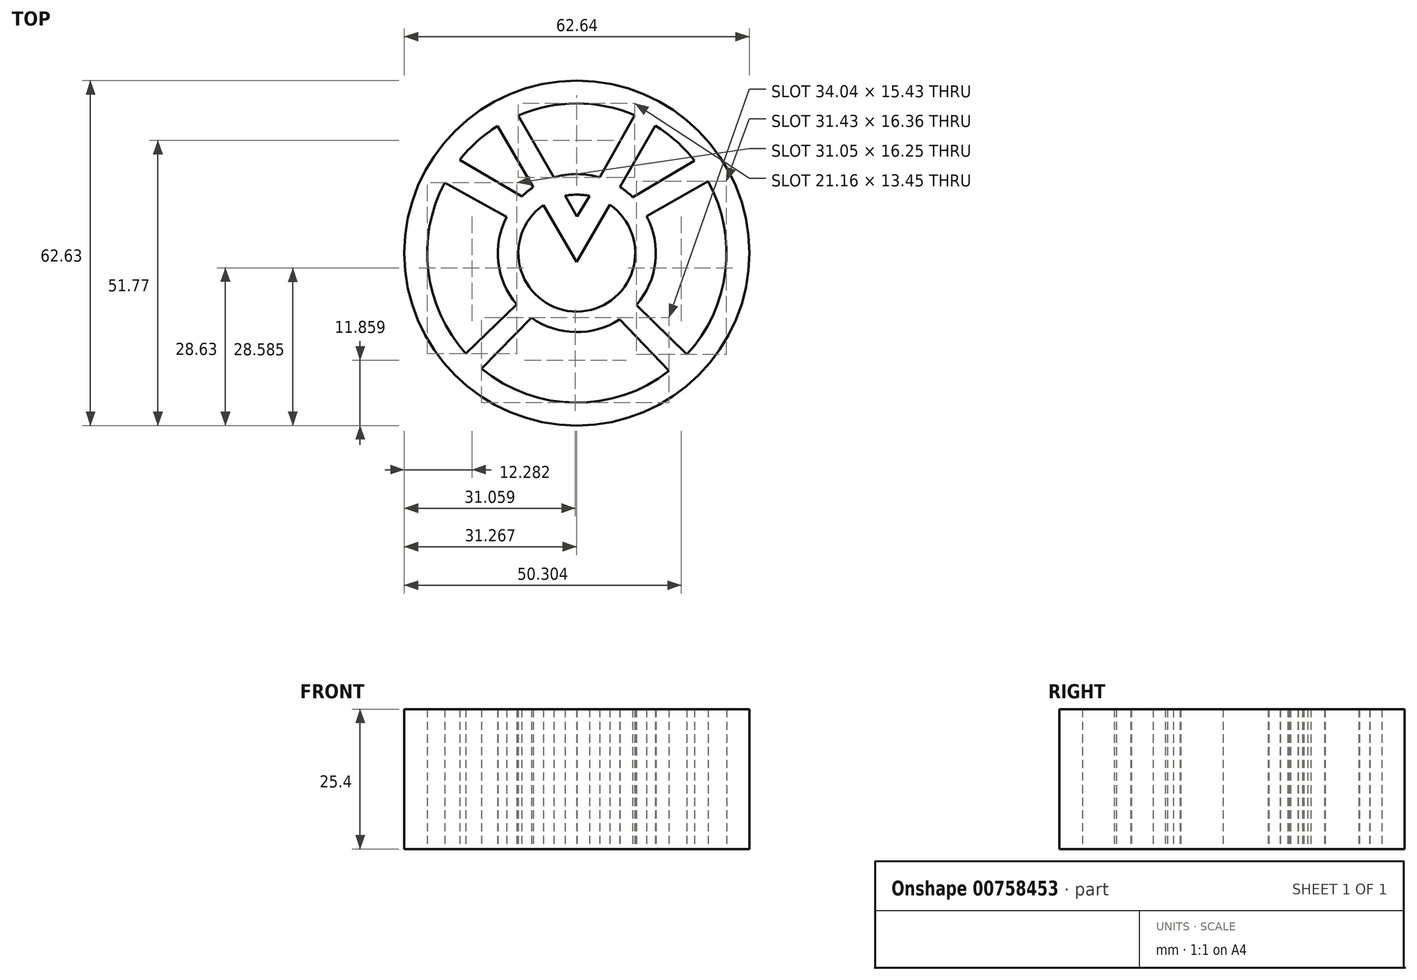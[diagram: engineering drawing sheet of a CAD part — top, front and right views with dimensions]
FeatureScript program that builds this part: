
annotation { "Feature Type Name" : "Feature", "Feature Type Description" : "" }
export const myFeature = defineFeature(function(context is Context, id is Id, definition is map)
    precondition{}
    {
        {
            var Q0;
            Q0=qCreatedBy(makeId("Top.planeOp"),FACE);
            var sketch = newSketch(context, id + "F0", { "sketchPlane" : qUnion([Q0])});
            skCircle(sketch, "E0", {"center": v(33.81, 37.33) * mm, "radius": 31.32 * mm});
            skArc(sketch, "E1", {"start": v(55.2, 54.1) * mm, "mid": v(51.91, 57.6) * mm, "end": v(48.06, 60.47) * mm});
            skLineSegment(sketch, "E2", {"start": v(48.06, 60.47) * mm, "end": v(41.65, 49.34) * mm});
            skLineSegment(sketch, "E3", {"start": v(33.81, 35.72) * mm, "end": v(27.77, 46.06) * mm});
            skArc(sketch, "E4", {"start": v(27.77, 46.06) * mm, "mid": v(33.85, 26.7) * mm, "end": v(39.79, 46.1) * mm});
            skArc(sketch, "E5", {"start": v(25.88, 49.29) * mm, "mid": v(24.8, 48.5) * mm, "end": v(23.8, 47.61) * mm});
            skLineSegment(sketch, "E6", {"start": v(23.18, 62.34) * mm, "end": v(29.66, 51.06) * mm});
            skLineSegment(sketch, "E7", {"start": v(44.33, 62.38) * mm, "end": v(37.98, 51.06) * mm});
            skLineSegment(sketch, "E8", {"start": v(55.2, 54.1) * mm, "end": v(43.95, 47.48) * mm});
            skLineSegment(sketch, "E9", {"start": v(57.66, 50.35) * mm, "end": v(46.5, 44.03) * mm});
            skLineSegment(sketch, "E10", {"start": v(53.8, 18.93) * mm, "end": v(44.62, 27.89) * mm});
            skLineSegment(sketch, "E11", {"start": v(50.57, 15.93) * mm, "end": v(41.57, 25.26) * mm});
            skLineSegment(sketch, "E12", {"start": v(16.53, 16.35) * mm, "end": v(25.56, 25.58) * mm});
            skLineSegment(sketch, "E13", {"start": v(13.68, 19.07) * mm, "end": v(22.9, 28.01) * mm});
            skLineSegment(sketch, "E14", {"start": v(21.07, 43.92) * mm, "end": v(9.83, 50.12) * mm});
            skLineSegment(sketch, "E15", {"start": v(12.54, 54.24) * mm, "end": v(23.8, 47.61) * mm});
            skLineSegment(sketch, "E16.trimOffspring", {"start": v(25.88, 49.29) * mm, "end": v(19.4, 60.37) * mm});
            skLineSegment(sketch, "E17", {"start": v(31.71, 47.74) * mm, "end": v(33.82, 43.96) * mm});
            skLineSegment(sketch, "E18", {"start": v(33.82, 43.96) * mm, "end": v(36.12, 47.7) * mm});
            skArc(sketch, "E19.trimOffspring", {"start": v(36.12, 47.7) * mm, "mid": v(33.92, 47.94) * mm, "end": v(31.71, 47.74) * mm});
            skLineSegment(sketch, "E20.trimOffspring", {"start": v(39.79, 46.1) * mm, "end": v(33.81, 35.72) * mm});
            skArc(sketch, "E21.trimOffspring", {"start": v(37.98, 51.06) * mm, "mid": v(33.82, 51.68) * mm, "end": v(29.66, 51.06) * mm});
            skArc(sketch, "E22.trimOffspring", {"start": v(43.95, 47.48) * mm, "mid": v(42.85, 48.47) * mm, "end": v(41.65, 49.34) * mm});
            skArc(sketch, "E23.trimOffspring", {"start": v(21.07, 43.92) * mm, "mid": v(19.56, 35.69) * mm, "end": v(22.9, 28.01) * mm});
            skArc(sketch, "E24.trimOffspring", {"start": v(44.62, 27.89) * mm, "mid": v(48.06, 35.67) * mm, "end": v(46.5, 44.03) * mm});
            skArc(sketch, "E25.trimOffspring", {"start": v(25.56, 25.58) * mm, "mid": v(33.52, 22.98) * mm, "end": v(41.57, 25.26) * mm});
            skArc(sketch, "E26.trimOffspring", {"start": v(44.33, 62.38) * mm, "mid": v(33.75, 64.5) * mm, "end": v(23.18, 62.34) * mm});
            skArc(sketch, "E27.trimOffspring", {"start": v(19.4, 60.37) * mm, "mid": v(15.71, 57.6) * mm, "end": v(12.54, 54.24) * mm});
            skArc(sketch, "E28.trimOffspring", {"start": v(9.83, 50.12) * mm, "mid": v(6.84, 33.99) * mm, "end": v(13.68, 19.07) * mm});
            skArc(sketch, "E29.trimOffspring", {"start": v(53.8, 18.93) * mm, "mid": v(60.79, 34.02) * mm, "end": v(57.66, 50.35) * mm});
            skArc(sketch, "E30.trimOffspring", {"start": v(16.53, 16.35) * mm, "mid": v(33.47, 10.15) * mm, "end": v(50.57, 15.93) * mm});
            skSolve(sketch);
        }
        {
            var Q0;
            Q0=makeQuery(id+"F0.imprint","IMPRINT",FACE,{"disambiguationData":[TD([[makeQuery(id+"F0.imprint","IMPRINT",EDGE,{"derivedFrom":sQuery(id+"F0.wireOp",EDGE,"E0")}),1.0]])]});
            extrude(context, id + "F1", {"entities" : qUnion([Q0]), "depth" : 25.4 * mm, "offsetDistance" : 25.4 * mm});
        }
    });
